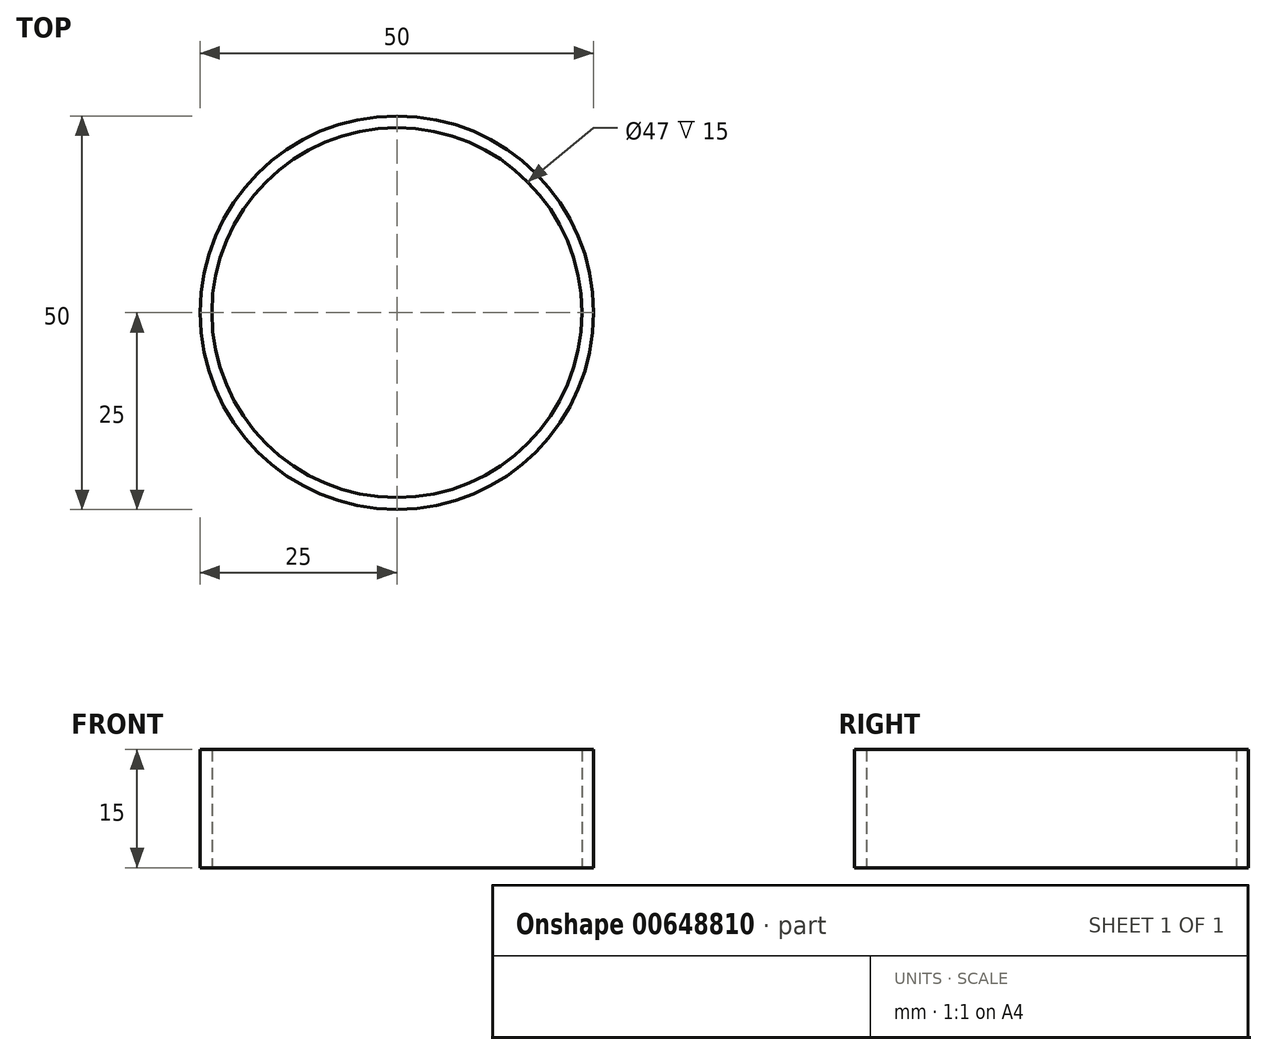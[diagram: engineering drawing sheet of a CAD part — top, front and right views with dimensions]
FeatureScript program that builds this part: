
annotation { "Feature Type Name" : "Feature", "Feature Type Description" : "" }
export const myFeature = defineFeature(function(context is Context, id is Id, definition is map)
    precondition{}
    {
        {
            var Q0;
            Q0=qCreatedBy(makeId("Top.planeOp"),FACE);
            var sketch = newSketch(context, id + "F0", { "sketchPlane" : qUnion([Q0])});
            skCircle(sketch, "E0", {"center": v(0, 0) * mm, "radius": 23.5 * mm});
            skCircle(sketch, "E1.0", {"center": v(0, 0) * mm, "radius": 25 * mm});
            skSolve(sketch);
        }
        {
            var Q0;
            Q0=makeQuery(id+"F0.imprint","IMPRINT",FACE,{"disambiguationData":[TD([[makeQuery(id+"F0.imprint","IMPRINT",EDGE,{"derivedFrom":sQuery(id+"F0.wireOp",EDGE,"E0")}),-1.0]])]});
            extrude(context, id + "F1", {"entities" : qUnion([Q0]), "endBound" : BoundingType.SYMMETRIC, "depth" : 15 * mm, "offsetDistance" : 25 * mm});
        }
    });
